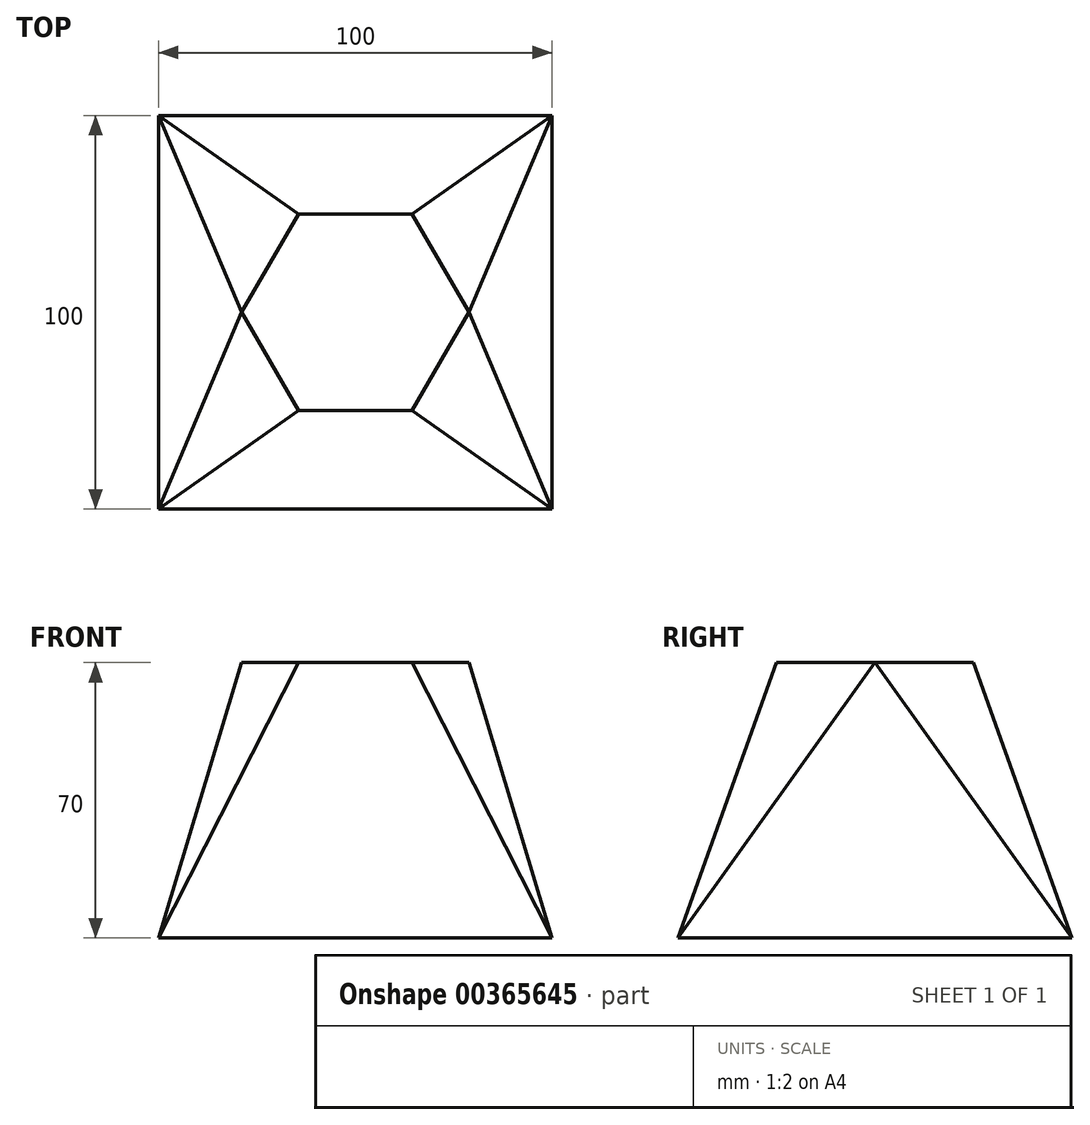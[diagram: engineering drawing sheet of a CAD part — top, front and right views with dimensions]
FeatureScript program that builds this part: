
annotation { "Feature Type Name" : "Feature", "Feature Type Description" : "" }
export const myFeature = defineFeature(function(context is Context, id is Id, definition is map)
    precondition{}
    {
        {
            var Q0;
            Q0=qCreatedBy(makeId("Top.planeOp"),FACE);
            var sketch = newSketch(context, id + "F0", { "sketchPlane" : qUnion([Q0])});
            skLineSegment(sketch, "E0.bottom", {"start": v(50, 50) * mm, "end": v(-50, 50) * mm});
            skLineSegment(sketch, "E0.top", {"start": v(50, -50) * mm, "end": v(-50, -50) * mm});
            skLineSegment(sketch, "E0.left", {"start": v(50, 50) * mm, "end": v(50, -50) * mm});
            skLineSegment(sketch, "E0.right", {"start": v(-50, 50) * mm, "end": v(-50, -50) * mm});
            skPoint(sketch, "E0.middle", {"position": v(0, 0) * mm});
            skSolve(sketch);
        }
        {
            var Q0;
            Q0=qCreatedBy(makeId("Top.planeOp"),FACE);
            cPlane(context, id + "F1", {"entities" : qUnion([Q0]), "cplaneType" : CPlaneType.OFFSET, "offset" : 70 * mm, "width" : 150 * mm, "height" : 150 * mm});
        }
        {
            var Q0;
            Q0=qCreatedBy(id+"F1.planeOp",FACE);
            var sketch = newSketch(context, id + "F2", { "sketchPlane" : qUnion([Q0])});
            skCircle(sketch, "E1.cCircle", {"center": v(0, 0) * mm, "radius": 28.87 * mm, "construction": true});
            skLineSegment(sketch, "E1.0", {"start": v(28.87, 0) * mm, "end": v(14.43, -25) * mm});
            skLineSegment(sketch, "E1.1", {"start": v(14.43, -25) * mm, "end": v(-14.43, -25) * mm});
            skLineSegment(sketch, "E1.2", {"start": v(-14.43, -25) * mm, "end": v(-28.87, 0) * mm});
            skLineSegment(sketch, "E1.3", {"start": v(-28.87, 0) * mm, "end": v(-14.43, 25) * mm});
            skLineSegment(sketch, "E1.4", {"start": v(-14.43, 25) * mm, "end": v(14.43, 25) * mm});
            skLineSegment(sketch, "E1.5", {"start": v(14.43, 25) * mm, "end": v(28.87, 0) * mm});
            skLineSegment(sketch, "E2", {"start": v(14.43, 25) * mm, "end": v(14.43, -25) * mm});
            skLineSegment(sketch, "E3", {"start": v(-14.43, 25) * mm, "end": v(-14.43, -25) * mm});
            skSolve(sketch);
        }
        {
            var Q0;
            Q0=makeQuery(id+"F2.imprint","IMPRINT",FACE,{"disambiguationData":[TD([[makeQuery(id+"F2.imprint","IMPRINT",EDGE,{"derivedFrom":sQuery(id+"F2.wireOp",EDGE,"E1.1")}),-1.0]])]});
            var Q1;
            Q1=makeQuery(id+"F0.imprint","IMPRINT",FACE,{"disambiguationData":[TD([[makeQuery(id+"F0.imprint","IMPRINT",EDGE,{"derivedFrom":sQuery(id+"F0.wireOp",EDGE,"E0.bottom")}),1.0]])]});
            loft(context, id + "F3", {"sheetProfilesArray" : [{ "sheetProfileEntities" : qUnion([Q0]) }, { "sheetProfileEntities" : qUnion([Q1]) }]});
        }
        {
            var Q1;
            Q1=makeQuery(id+"F2.imprint","IMPRINT",FACE,{"disambiguationData":[TD([[makeQuery(id+"F2.imprint","IMPRINT",EDGE,{"derivedFrom":sQuery(id+"F2.wireOp",EDGE,"E1.0")}),-1.0]])]});
            var Q2;
            Q2=makeQuery(id+"F3.opLoft","MID_CAP_VERTEX",VERTEX,{"disambiguationData":[OSD([sQuery(id+"F0.wireOp",EDGE,"E0.bottom"),sQuery(id+"F0.wireOp",EDGE,"E0.left")])],"capPos":1.0});
            loft(context, id + "F4", {"operationType" : NewBodyOperationType.ADD, "sheetProfilesArray" : [{ "sheetProfileEntities" : qUnion([Q1]) }, { "sheetProfileEntities" : qUnion([Q2]) }]});
        }
        {
            var Q1;
            Q1=makeQuery(id+"F2.imprint","IMPRINT",FACE,{"disambiguationData":[TD([[makeQuery(id+"F2.imprint","IMPRINT",EDGE,{"derivedFrom":sQuery(id+"F2.wireOp",EDGE,"E1.0")}),-1.0]])]});
            var Q2;
            Q2=makeQuery(id+"F3.opLoft","MID_CAP_VERTEX",VERTEX,{"disambiguationData":[OSD([sQuery(id+"F0.wireOp",EDGE,"E0.top"),sQuery(id+"F0.wireOp",EDGE,"E0.left")])],"capPos":1.0});
            loft(context, id + "F5", {"operationType" : NewBodyOperationType.ADD, "sheetProfilesArray" : [{ "sheetProfileEntities" : qUnion([Q1]) }, { "sheetProfileEntities" : qUnion([Q2]) }]});
        }
        {
            var Q1;
            Q1=makeQuery(id+"F5.opLoft","SWEPT_FACE",FACE,{"disambiguationData":[OSD([sQuery(id+"F2.wireOp",EDGE,"E1.0"),sQuery(id+"F2.wireOp",EDGE,"E1.4"),sQuery(id+"F2.wireOp",EDGE,"E1.5"),sQuery(id+"F2.wireOp",EDGE,"E2")])]});
            var Q2;
            Q2=makeQuery(id+"F4.opLoft","SWEPT_FACE",FACE,{"disambiguationData":[OSD([sQuery(id+"F2.wireOp",EDGE,"E1.0"),sQuery(id+"F2.wireOp",EDGE,"E1.1"),sQuery(id+"F2.wireOp",EDGE,"E1.5"),sQuery(id+"F2.wireOp",EDGE,"E2")])]});
            var Q3;
            Q3=makeQuery(id+"F3.opLoft","MID_CAP_EDGE",EDGE,{"disambiguationData":[OSD([sQuery(id+"F0.wireOp",EDGE,"E0.bottom"),sQuery(id+"F0.wireOp",EDGE,"E0.top"),sQuery(id+"F0.wireOp",EDGE,"E0.left")])],"capPos":1.0});
            loft(context, id + "F6", {"operationType" : NewBodyOperationType.ADD, "addGuides" : true, "sheetProfilesArray" : [{ "sheetProfileEntities" : qUnion([Q1]) }, { "sheetProfileEntities" : qUnion([Q2]) }], "guidesArray" : [{ "guideEntities" : qUnion([Q3]), "guideDerivativeType" : LoftGuideDerivativeType.DEFAULT, "guideDerivativeMagnitude" : 1 }]});
        }
        {
            var Q1;
            Q1=makeQuery(id+"F2.imprint","IMPRINT",FACE,{"disambiguationData":[TD([[makeQuery(id+"F2.imprint","IMPRINT",EDGE,{"derivedFrom":sQuery(id+"F2.wireOp",EDGE,"E1.2")}),-1.0]])]});
            var Q2;
            Q2=makeQuery(id+"F3.opLoft","MID_CAP_VERTEX",VERTEX,{"disambiguationData":[OSD([sQuery(id+"F0.wireOp",EDGE,"E0.bottom"),sQuery(id+"F0.wireOp",EDGE,"E0.right")])],"capPos":1.0});
            loft(context, id + "F7", {"operationType" : NewBodyOperationType.ADD, "sheetProfilesArray" : [{ "sheetProfileEntities" : qUnion([Q1]) }, { "sheetProfileEntities" : qUnion([Q2]) }]});
        }
        {
            var Q1;
            Q1=makeQuery(id+"F2.imprint","IMPRINT",FACE,{"disambiguationData":[TD([[makeQuery(id+"F2.imprint","IMPRINT",EDGE,{"derivedFrom":sQuery(id+"F2.wireOp",EDGE,"E1.2")}),-1.0]])]});
            var Q2;
            Q2=makeQuery(id+"F3.opLoft","MID_CAP_VERTEX",VERTEX,{"disambiguationData":[OSD([sQuery(id+"F0.wireOp",EDGE,"E0.top"),sQuery(id+"F0.wireOp",EDGE,"E0.right")])],"capPos":1.0});
            loft(context, id + "F8", {"operationType" : NewBodyOperationType.ADD, "sheetProfilesArray" : [{ "sheetProfileEntities" : qUnion([Q1]) }, { "sheetProfileEntities" : qUnion([Q2]) }]});
        }
        {
            var Q1;
            Q1=makeQuery(id+"F7.opLoft","SWEPT_FACE",FACE,{"disambiguationData":[OSD([sQuery(id+"F2.wireOp",EDGE,"E1.1"),sQuery(id+"F2.wireOp",EDGE,"E1.2"),sQuery(id+"F2.wireOp",EDGE,"E1.3"),sQuery(id+"F2.wireOp",EDGE,"E3")])]});
            var Q2;
            Q2=makeQuery(id+"F8.opLoft","SWEPT_FACE",FACE,{"disambiguationData":[OSD([sQuery(id+"F2.wireOp",EDGE,"E1.2"),sQuery(id+"F2.wireOp",EDGE,"E1.3"),sQuery(id+"F2.wireOp",EDGE,"E1.4"),sQuery(id+"F2.wireOp",EDGE,"E3")])]});
            var Q3;
            Q3=makeQuery(id+"F3.opLoft","MID_CAP_EDGE",EDGE,{"disambiguationData":[OSD([sQuery(id+"F0.wireOp",EDGE,"E0.bottom"),sQuery(id+"F0.wireOp",EDGE,"E0.top"),sQuery(id+"F0.wireOp",EDGE,"E0.right")])],"capPos":1.0});
            loft(context, id + "F9", {"operationType" : NewBodyOperationType.ADD, "addGuides" : true, "sheetProfilesArray" : [{ "sheetProfileEntities" : qUnion([Q1]) }, { "sheetProfileEntities" : qUnion([Q2]) }], "guidesArray" : [{ "guideEntities" : qUnion([Q3]), "guideDerivativeType" : LoftGuideDerivativeType.DEFAULT, "guideDerivativeMagnitude" : 1 }]});
        }
    });
